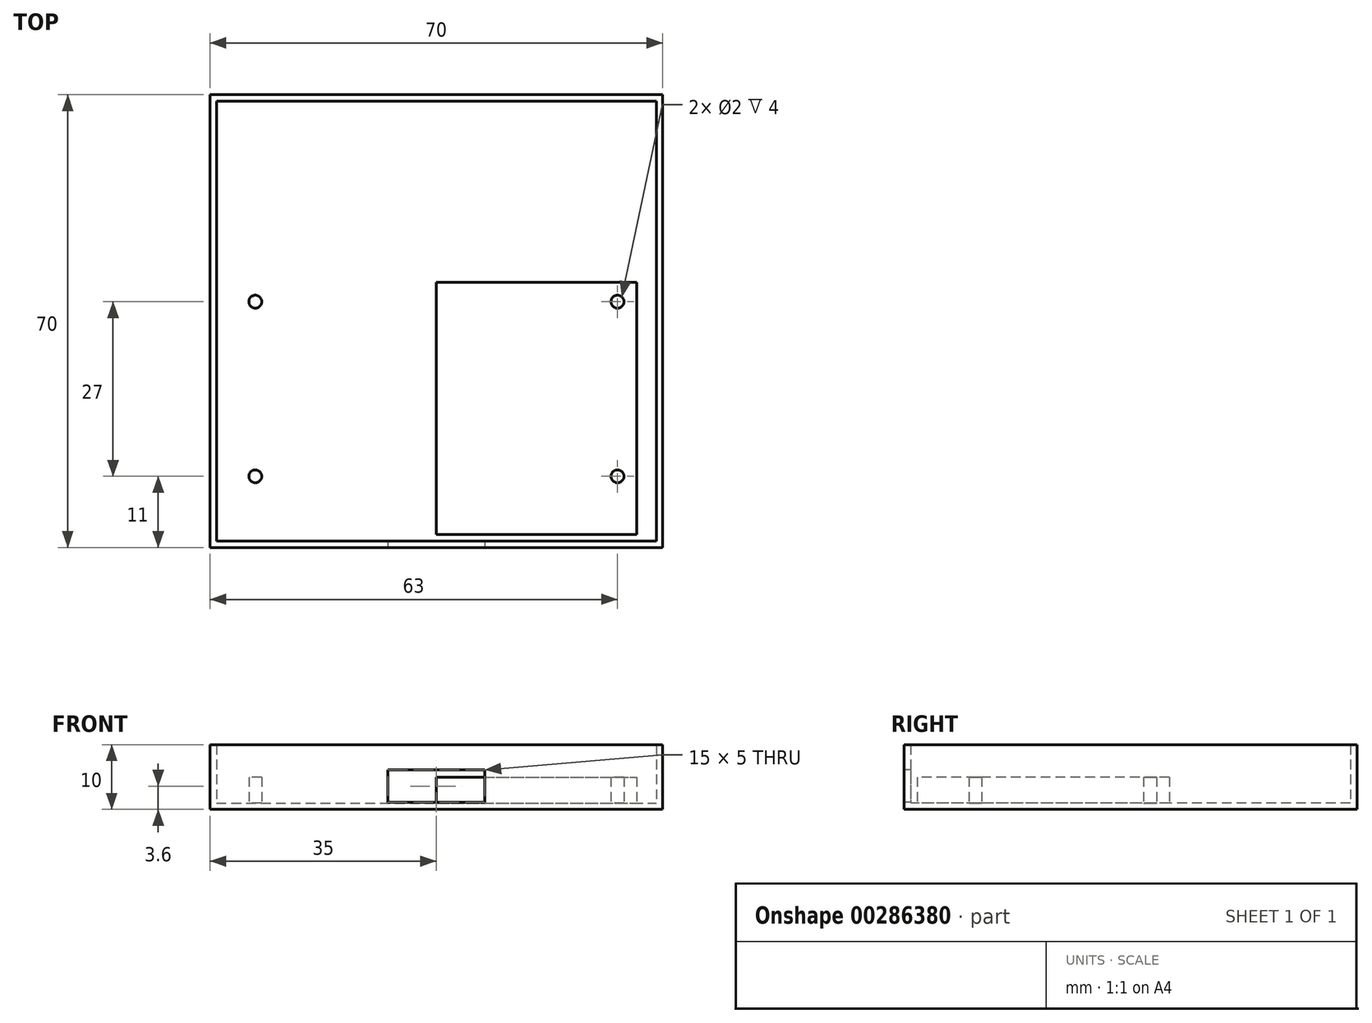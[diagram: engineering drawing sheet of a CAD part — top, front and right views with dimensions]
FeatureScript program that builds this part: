
annotation { "Feature Type Name" : "Feature", "Feature Type Description" : "" }
export const myFeature = defineFeature(function(context is Context, id is Id, definition is map)
    precondition{}
    {
        {
            var Q0;
            Q0=qCreatedBy(makeId("Top.planeOp"),FACE);
            var sketch = newSketch(context, id + "F0", { "sketchPlane" : qUnion([Q0])});
            skLineSegment(sketch, "E0.bottom", {"start": v(0, 0) * mm, "end": v(-70, 0) * mm});
            skLineSegment(sketch, "E0.top", {"start": v(0, 70) * mm, "end": v(-70, 70) * mm});
            skLineSegment(sketch, "E0.left", {"start": v(0, 0) * mm, "end": v(0, 70) * mm});
            skLineSegment(sketch, "E0.right", {"start": v(-70, 0) * mm, "end": v(-70, 70) * mm});
            skSolve(sketch);
        }
        {
            var Q0;
            Q0=makeQuery(id+"F0.imprint","IMPRINT",FACE,{"disambiguationData":[TD([[makeQuery(id+"F0.imprint","IMPRINT",EDGE,{"derivedFrom":sQuery(id+"F0.wireOp",EDGE,"E0.bottom")}),-1.0]])]});
            extrude(context, id + "F1", {"entities" : qUnion([Q0]), "depth" : 1 * mm});
        }
        {
            var Q0;
            Q0=makeQuery(id+"F1.opExtrude","CAP_FACE",FACE,{"disambiguationData":[OSD([sQuery(id+"F0.wireOp",EDGE,"E0.bottom"),sQuery(id+"F0.wireOp",EDGE,"E0.top"),sQuery(id+"F0.wireOp",EDGE,"E0.left"),sQuery(id+"F0.wireOp",EDGE,"E0.right")])],"isStart":false});
            var sketch = newSketch(context, id + "F2", { "sketchPlane" : qUnion([Q0])});
            skLineSegment(sketch, "E1.bottom", {"start": v(-69, 69) * mm, "end": v(-1, 69) * mm});
            skLineSegment(sketch, "E1.top", {"start": v(-69, 1) * mm, "end": v(-1, 1) * mm});
            skLineSegment(sketch, "E1.left", {"start": v(-69, 69) * mm, "end": v(-69, 1) * mm});
            skLineSegment(sketch, "E1.right", {"start": v(-1, 69) * mm, "end": v(-1, 1) * mm});
            skSolve(sketch);
        }
        {
            var Q0;
            Q0=makeQuery(id+"F2.imprint","IMPRINT",FACE,{"disambiguationData":[TD([[makeQuery(id+"F2.imprint","IMPRINT",EDGE,{"derivedFrom":sQuery(id+"F2.wireOp",EDGE,"E1.bottom")}),1.0]])]});
            extrude(context, id + "F3", {"entities" : qUnion([Q0]), "operationType" : NewBodyOperationType.ADD, "depth" : 9 * mm});
        }
        {
            var Q0;
            {var subQ0=sQuery(id+"F0.wireOp",EDGE,"E0.bottom");Q0=makeQuery(id+"F3.boolean.opBoolean","MERGE",FACE,{"derivedFrom":[makeQuery(id+"F1.opExtrude","SWEPT_FACE",FACE,{"disambiguationData":[OSD([subQ0])]}),makeQuery(id+"F3.opExtrude","SWEPT_FACE",FACE,{"disambiguationData":[OSD([subQ0])]})]});}
            var sketch = newSketch(context, id + "F4", { "sketchPlane" : qUnion([Q0])});
            skLineSegment(sketch, "E2.bottom", {"start": v(-42.5, 6.1) * mm, "end": v(-27.5, 6.1) * mm});
            skLineSegment(sketch, "E2.top", {"start": v(-42.5, 1.1) * mm, "end": v(-27.5, 1.1) * mm});
            skLineSegment(sketch, "E2.left", {"start": v(-42.5, 6.1) * mm, "end": v(-42.5, 1.1) * mm});
            skLineSegment(sketch, "E2.right", {"start": v(-27.5, 6.1) * mm, "end": v(-27.5, 1.1) * mm});
            skSolve(sketch);
        }
        {
            var Q0;
            Q0=makeQuery(id+"F4.imprint","IMPRINT",FACE,{"disambiguationData":[TD([[makeQuery(id+"F4.imprint","IMPRINT",EDGE,{"derivedFrom":sQuery(id+"F4.wireOp",EDGE,"E2.bottom")}),-1.0]])]});
            extrude(context, id + "F5", {"entities" : qUnion([Q0]), "operationType" : NewBodyOperationType.REMOVE, "oppositeDirection" : true, "depth" : 1 * mm});
        }
        {
            var Q0;
            Q0=makeQuery(id+"F1.opExtrude","CAP_FACE",FACE,{"disambiguationData":[OSD([sQuery(id+"F0.wireOp",EDGE,"E0.bottom"),sQuery(id+"F0.wireOp",EDGE,"E0.top"),sQuery(id+"F0.wireOp",EDGE,"E0.left"),sQuery(id+"F0.wireOp",EDGE,"E0.right")])],"isStart":false});
            var sketch = newSketch(context, id + "F6", { "sketchPlane" : qUnion([Q0])});
            skLineSegment(sketch, "E3.bottom", {"start": v(-66, 41) * mm, "end": v(-4, 41) * mm});
            skLineSegment(sketch, "E3.top", {"start": v(-66, 2) * mm, "end": v(-4, 2) * mm});
            skLineSegment(sketch, "E3.left", {"start": v(-66, 41) * mm, "end": v(-66, 2) * mm});
            skLineSegment(sketch, "E3.right", {"start": v(-4, 41) * mm, "end": v(-4, 2) * mm});
            skCircle(sketch, "E4", {"center": v(-63, 11) * mm, "radius": 1 * mm});
            skCircle(sketch, "E5", {"center": v(-63, 38) * mm, "radius": 1 * mm});
            skLineSegment(sketch, "E6", {"start": v(-35, 41) * mm, "end": v(-35, 2) * mm});
            skCircle(sketch, "E7.MirrorC", {"center": v(-7, 38) * mm, "radius": 1 * mm});
            skCircle(sketch, "E8.MirrorC", {"center": v(-7, 11) * mm, "radius": 1 * mm});
            skSolve(sketch);
        }
        {
            var Q0;
            Q0=makeQuery(id+"F6.imprint","IMPRINT",FACE,{"disambiguationData":[TD([[makeQuery(id+"F6.imprint","IMPRINT",EDGE,{"derivedFrom":sQuery(id+"F6.wireOp",EDGE,"E5")}),1.0]])]});
            var Q1;
            Q1=makeQuery(id+"F6.imprint","IMPRINT",FACE,{"disambiguationData":[TD([[makeQuery(id+"F6.imprint","IMPRINT",EDGE,{"derivedFrom":sQuery(id+"F6.wireOp",EDGE,"E7.MirrorC")}),-1.0]])]});
            var Q2;
            Q2=makeQuery(id+"F6.imprint","IMPRINT",FACE,{"disambiguationData":[TD([[makeQuery(id+"F6.imprint","IMPRINT",EDGE,{"derivedFrom":sQuery(id+"F6.wireOp",EDGE,"E8.MirrorC")}),-1.0]])]});
            var Q3;
            Q3=makeQuery(id+"F6.imprint","IMPRINT",FACE,{"disambiguationData":[TD([[makeQuery(id+"F6.imprint","IMPRINT",EDGE,{"derivedFrom":sQuery(id+"F6.wireOp",EDGE,"E4")}),1.0]])]});
            extrude(context, id + "F7", {"entities" : qUnion([Q0, Q1, Q2, Q3]), "operationType" : NewBodyOperationType.ADD, "depth" : 4 * mm});
        }
    });
